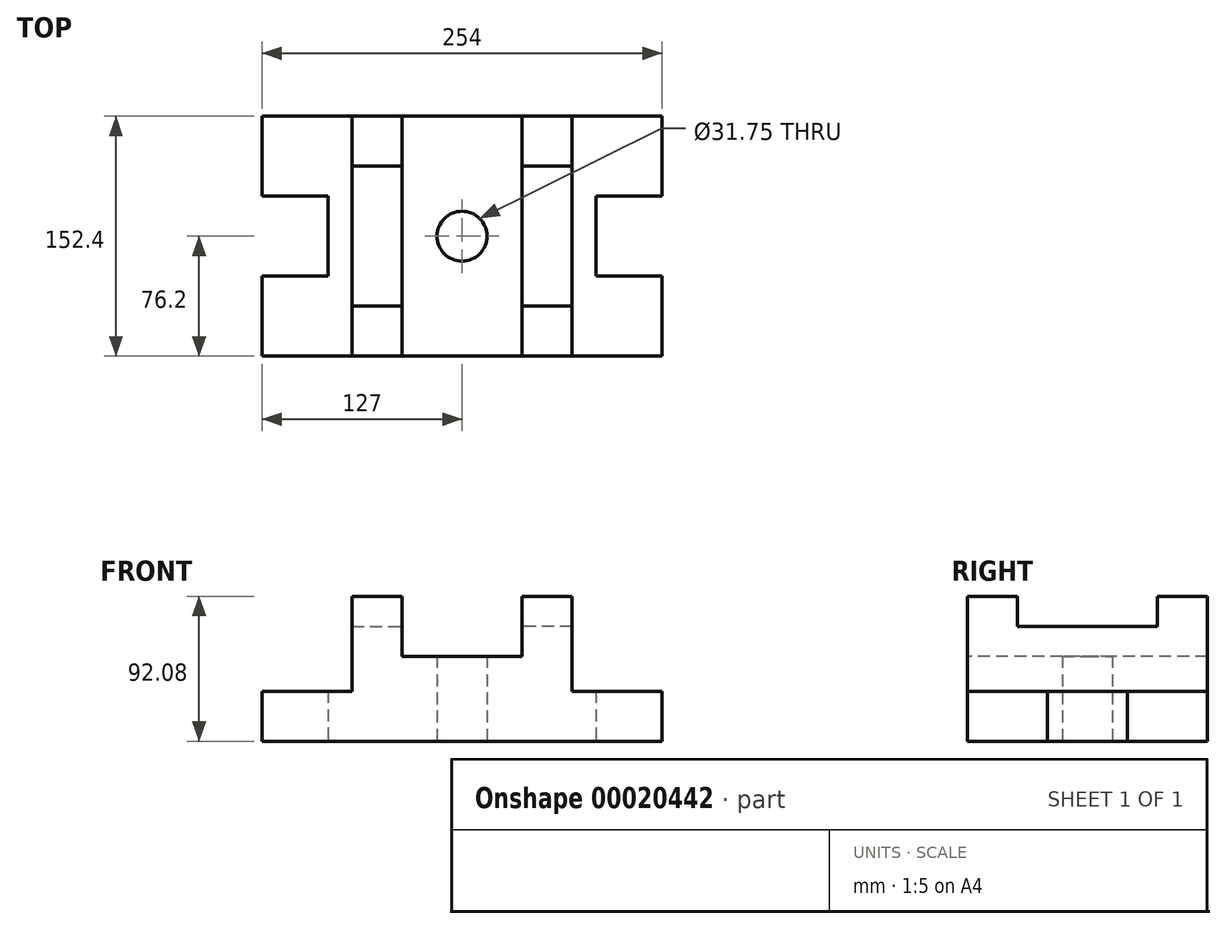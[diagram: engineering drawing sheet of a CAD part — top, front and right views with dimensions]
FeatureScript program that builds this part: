
annotation { "Feature Type Name" : "Feature", "Feature Type Description" : "" }
export const myFeature = defineFeature(function(context is Context, id is Id, definition is map)
    precondition{}
    {
        {
            var Q0;
            Q0=qCreatedBy(makeId("Top.planeOp"),FACE);
            var sketch = newSketch(context, id + "F0", { "sketchPlane" : qUnion([Q0])});
            skLineSegment(sketch, "E0.bottom", {"start": v(-127, 76.2) * mm, "end": v(0, 76.2) * mm});
            skLineSegment(sketch, "E0.top", {"start": v(-127, -76.2) * mm, "end": v(0, -76.2) * mm});
            skLineSegment(sketch, "E0.left", {"start": v(-127, 76.2) * mm, "end": v(-127, 25.4) * mm});
            skLineSegment(sketch, "E0.right", {"start": v(0, 76.2) * mm, "end": v(0, -76.2) * mm});
            skLineSegment(sketch, "E1.bottom", {"start": v(-127, 25.4) * mm, "end": v(-85.1, 25.4) * mm});
            skLineSegment(sketch, "E1.top", {"start": v(-127, -25.4) * mm, "end": v(-85.1, -25.4) * mm});
            skLineSegment(sketch, "E1.left", {"start": v(-127, 25.4) * mm, "end": v(-127, 25.4) * mm});
            skLineSegment(sketch, "E1.right", {"start": v(-85.1, 25.4) * mm, "end": v(-85.1, -25.4) * mm});
            skLineSegment(sketch, "E2.trimOffspring", {"start": v(-127, -25.4) * mm, "end": v(-127, -76.2) * mm});
            skPoint(sketch, "E3.orphan", {"position": v(-127, 0) * mm});
            skSolve(sketch);
        }
        {
            var Q0;
            Q0 = qSketchRegion(id + "F0", true);
            extrude(context, id + "F1", {"entities" : qUnion([Q0]), "depth" : 31.75 * mm});
        }
        {
            var Q0;
            Q0=makeQuery(id+"F1.opExtrude","CAP_FACE",FACE,{"disambiguationData":[OSD([sQuery(id+"F0.wireOp",EDGE,"E0.bottom"),sQuery(id+"F0.wireOp",EDGE,"E0.top"),sQuery(id+"F0.wireOp",EDGE,"E0.left"),sQuery(id+"F0.wireOp",EDGE,"E0.right"),sQuery(id+"F0.wireOp",EDGE,"E1.bottom"),sQuery(id+"F0.wireOp",EDGE,"E1.top"),sQuery(id+"F0.wireOp",EDGE,"E1.right"),sQuery(id+"F0.wireOp",EDGE,"E2.trimOffspring")])],"isStart":false});
            var sketch = newSketch(context, id + "F2", { "sketchPlane" : qUnion([Q0])});
            skArc(sketch, "E4", {"start": v(0, 15.88) * mm, "mid": v(-15.88, 0) * mm, "end": v(0, -15.88) * mm});
            skLineSegment(sketch, "E5", {"start": v(-69.85, 76.2) * mm, "end": v(-69.85, -76.2) * mm});
            skLineSegment(sketch, "E6", {"start": v(-127, 76.2) * mm, "end": v(-69.85, 76.2) * mm});
            skLineSegment(sketch, "E7", {"start": v(-69.85, 76.2) * mm, "end": v(-38.1, 76.2) * mm});
            skLineSegment(sketch, "E8", {"start": v(-38.1, 76.2) * mm, "end": v(-38.1, -76.2) * mm});
            skLineSegment(sketch, "E9", {"start": v(-69.85, 44.45) * mm, "end": v(-38.1, 44.45) * mm});
            skLineSegment(sketch, "E10", {"start": v(-69.85, 76.2) * mm, "end": v(-69.85, 44.45) * mm});
            skLineSegment(sketch, "E11.MirrorCS", {"start": v(-69.85, -44.45) * mm, "end": v(-38.1, -44.45) * mm});
            skLineSegment(sketch, "E12.MirrorCS", {"start": v(-69.85, -76.2) * mm, "end": v(-38.1, -76.2) * mm});
            skSolve(sketch);
        }
        {
            var Q0;
            {var subQ2=sQuery(id+"F2.wireOp",EDGE,"E7");Q0=makeQuery(id+"F2.imprint","IMPRINT",FACE,{"disambiguationData":[TD([[makeQuery(id+"F2.imprint","IMPRINT",EDGE,{"derivedFrom":subQ2}),-1.0]])]});}
            var Q1;
            {var subQ1=sQuery(id+"F2.wireOp",EDGE,"E11.MirrorCS");Q1=makeQuery(id+"F2.imprint","IMPRINT",FACE,{"disambiguationData":[TD([[makeQuery(id+"F2.imprint","IMPRINT",EDGE,{"derivedFrom":subQ1}),-1.0]])]});}
            extrude(context, id + "F3", {"entities" : qUnion([Q0, Q1]), "operationType" : NewBodyOperationType.ADD, "depth" : 60.32 * mm});
        }
        {
            var Q0;
            {var subQ1=sQuery(id+"F2.wireOp",EDGE,"E9");Q0=makeQuery(id+"F2.imprint","IMPRINT",FACE,{"disambiguationData":[TD([[makeQuery(id+"F2.imprint","IMPRINT",EDGE,{"derivedFrom":subQ1}),-1.0]])]});}
            extrude(context, id + "F4", {"entities" : qUnion([Q0]), "operationType" : NewBodyOperationType.ADD, "depth" : 41.27 * mm});
        }
        {
            var Q0;
            {var subQ1=sQuery(id+"F2.wireOp",EDGE,"E4");Q0=makeQuery(id+"F2.imprint","IMPRINT",FACE,{"disambiguationData":[TD([[makeQuery(id+"F2.imprint","IMPRINT",EDGE,{"derivedFrom":subQ1}),-1.0]])]});}
            extrude(context, id + "F5", {"entities" : qUnion([Q0]), "operationType" : NewBodyOperationType.ADD, "depth" : 22.22 * mm});
        }
        {
            var Q0;
            {var subQ1=sQuery(id+"F2.wireOp",EDGE,"E4");Q0=makeQuery(id+"F2.imprint","IMPRINT",FACE,{"disambiguationData":[TD([[makeQuery(id+"F2.imprint","IMPRINT",EDGE,{"derivedFrom":subQ1}),1.0]])]});}
            extrude(context, id + "F6", {"entities" : qUnion([Q0]), "operationType" : NewBodyOperationType.REMOVE, "oppositeDirection" : true, "depth" : 37.3 * mm});
        }
        {
            var Q0;
            Q0=makeQuery(id+"F1.opExtrude","SWEPT_BODY",BODY,{"disambiguationData":[OSD([sQuery(id+"F0.wireOp",EDGE,"E0.bottom"),sQuery(id+"F0.wireOp",EDGE,"E0.top"),sQuery(id+"F0.wireOp",EDGE,"E0.left"),sQuery(id+"F0.wireOp",EDGE,"E0.right"),sQuery(id+"F0.wireOp",EDGE,"E1.bottom"),sQuery(id+"F0.wireOp",EDGE,"E1.top"),sQuery(id+"F0.wireOp",EDGE,"E1.right"),sQuery(id+"F0.wireOp",EDGE,"E2.trimOffspring")])]});
            var Q1;
            {var subQ0=sQuery(id+"F0.wireOp",EDGE,"E0.right");var subQ1=makeQuery(id+"F1.opExtrude","CAP_EDGE",EDGE,{"disambiguationData":[OSD([subQ0])],"isStart":false});var subQ3=sQuery(id+"F0.wireOp",EDGE,"E0.bottom");var subQ4=sQuery(id+"F0.wireOp",EDGE,"E0.top");Q1=makeQuery(id+"F6.boolean.opBoolean","SPLIT",FACE,{"disambiguationData":[TD([makeQuery(id+"F1.opExtrude","SWEPT_FACE",FACE,{"disambiguationData":[OSD([subQ4])]})])],"derivedFrom":makeQuery(id+"F5.boolean.opBoolean","MERGE",FACE,{"derivedFrom":[makeQuery(id+"F1.opExtrude","SWEPT_FACE",FACE,{"disambiguationData":[OSD([subQ0])]}),makeQuery(id+"F5.opExtrude","SWEPT_FACE",FACE,{"disambiguationData":[OSD([subQ0]),TDD([makeQuery(id+"F2.imprint","IMPRINT",EDGE,{"disambiguationData":[TD([[makeQuery(id+"F2.imprint","INTERSECT",VERTEX,{"derivedFrom":[makeQuery(id+"F1.opExtrude","CAP_EDGE",EDGE,{"disambiguationData":[OSD([subQ3])],"isStart":false}),subQ1]}),-1.0]])],"derivedFrom":subQ1})])]}),makeQuery(id+"F5.opExtrude","SWEPT_FACE",FACE,{"disambiguationData":[OSD([subQ0]),TDD([makeQuery(id+"F2.imprint","IMPRINT",EDGE,{"disambiguationData":[TD([[makeQuery(id+"F2.imprint","INTERSECT",VERTEX,{"derivedFrom":[makeQuery(id+"F1.opExtrude","CAP_EDGE",EDGE,{"disambiguationData":[OSD([subQ4])],"isStart":false}),subQ1]}),1.0]])],"derivedFrom":subQ1})])]})]})});}
            mirror(context, id + "F7", {"operationType" : NewBodyOperationType.ADD, "entities" : qUnion([Q0]), "mirrorPlane" : qUnion([Q1])});
        }
    });
